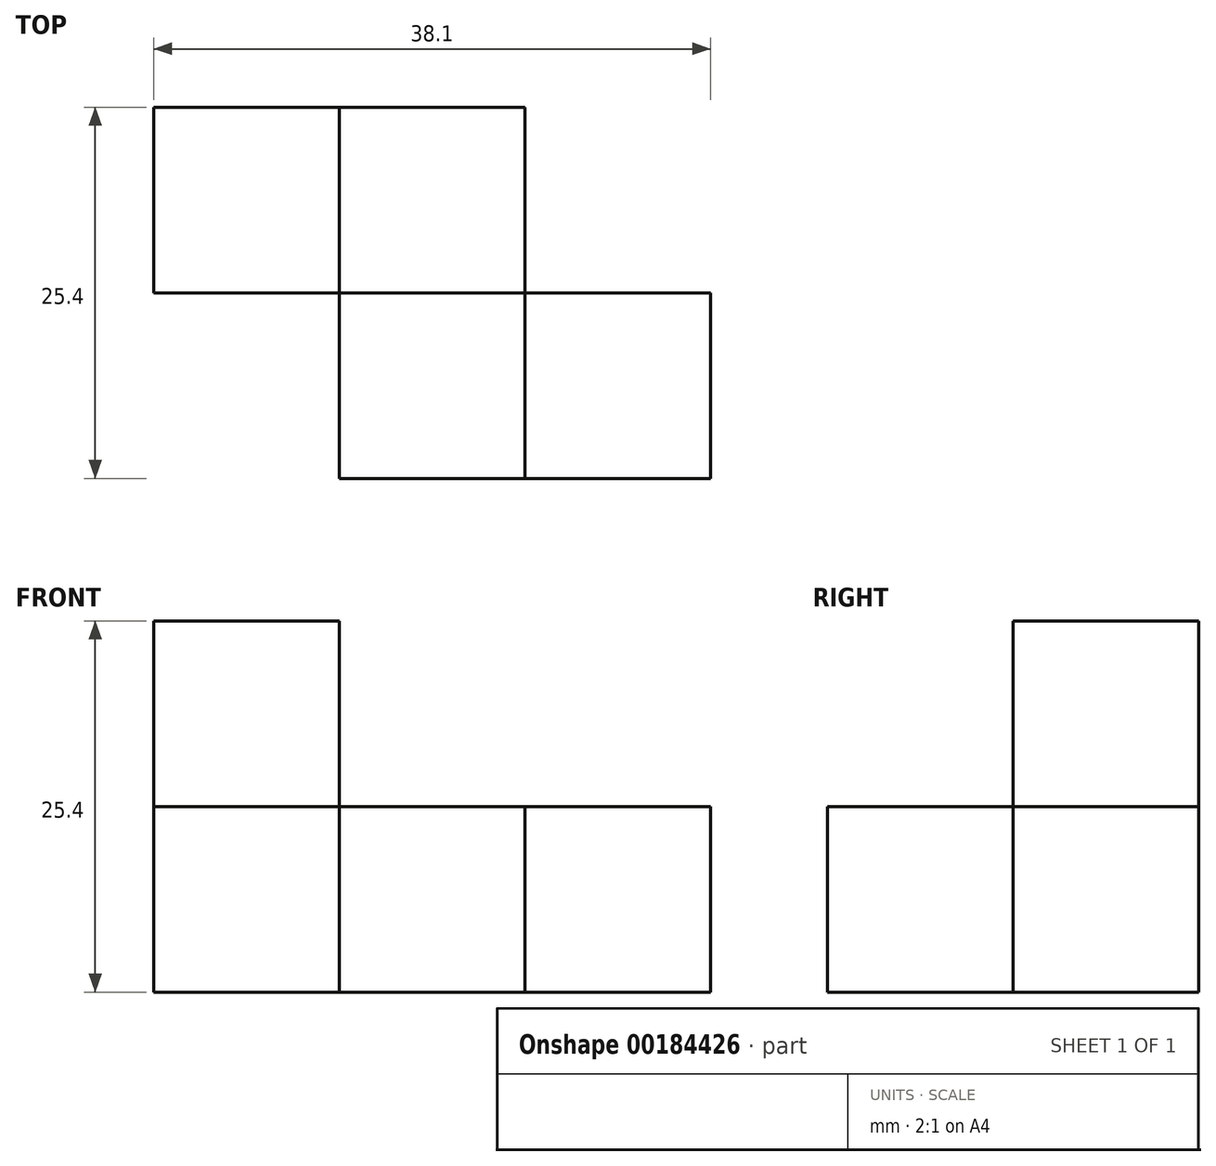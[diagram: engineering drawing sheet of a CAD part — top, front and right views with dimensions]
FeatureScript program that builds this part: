
annotation { "Feature Type Name" : "Feature", "Feature Type Description" : "" }
export const myFeature = defineFeature(function(context is Context, id is Id, definition is map)
    precondition{}
    {
        {
            var Q0;
            Q0=qCreatedBy(makeId("Front.planeOp"),FACE);
            var sketch = newSketch(context, id + "F0", { "sketchPlane" : qUnion([Q0])});
            skLineSegment(sketch, "E0.bottom", {"start": v(-58.66, 0) * mm, "end": v(-45.96, 0) * mm});
            skLineSegment(sketch, "E0.top", {"start": v(-58.66, -12.7) * mm, "end": v(-45.96, -12.7) * mm});
            skLineSegment(sketch, "E0.left", {"start": v(-58.66, 0) * mm, "end": v(-58.66, -12.7) * mm});
            skLineSegment(sketch, "E0.right", {"start": v(-45.96, 0) * mm, "end": v(-45.96, -12.7) * mm});
            skSolve(sketch);
        }
        {
            var Q0;
            Q0 = qSketchRegion(id + "F0", true);
            extrude(context, id + "F1", {"entities" : qUnion([Q0]), "depth" : 12.7 * mm});
        }
        {
            var Q0;
            Q0=makeQuery(id+"F1.opExtrude","SWEPT_EDGE",EDGE,{"disambiguationData":[OSD([sQuery(id+"F0.wireOp",EDGE,"E0.bottom"),sQuery(id+"F0.wireOp",EDGE,"E0.right")])]});
            cPoint(context, id + "F2", {"entities" : qUnion([Q0]), "parameter" : 0.5});
        }
        {
            var Q0;
            Q0=makeQuery(id+"F1.opExtrude","SWEPT_EDGE",EDGE,{"disambiguationData":[OSD([sQuery(id+"F0.wireOp",EDGE,"E0.bottom"),sQuery(id+"F0.wireOp",EDGE,"E0.left")])]});
            cPoint(context, id + "F3", {"entities" : qUnion([Q0]), "parameter" : 0.5});
        }
        {
            var Q0;
            Q0=makeQuery(id+"F1.opExtrude","SWEPT_BODY",BODY,{"disambiguationData":[OSD([sQuery(id+"F0.wireOp",EDGE,"E0.bottom"),sQuery(id+"F0.wireOp",EDGE,"E0.top"),sQuery(id+"F0.wireOp",EDGE,"E0.left"),sQuery(id+"F0.wireOp",EDGE,"E0.right")])]});
            var Q1;
            Q1 = qCreatedBy(id + "F2" ,VERTEX);
            var Q2;
            Q2 = qCreatedBy(id + "F3" ,VERTEX);
            transform(context, id + "F4", {"entities" : qUnion([Q0]), "transformType" : TransformType.TRANSLATION_ENTITY, "oppositeDirectionEntity" : false, "transformLine" : qUnion([Q1, Q2]), "makeCopy" : true});
        }
        {
            var Q0;
            Q0=makeQuery(id+"F4.opPattern","COPY",EDGE,{"derivedFrom":makeQuery(id+"F1.opExtrude","CAP_EDGE",EDGE,{"disambiguationData":[OSD([sQuery(id+"F0.wireOp",EDGE,"E0.bottom")])],"isStart":false}),"instanceName":"1"});
            cPoint(context, id + "F5", {"entities" : qUnion([Q0]), "parameter" : 0.5});
        }
        {
            var Q0;
            Q0=makeQuery(id+"F4.opPattern","COPY",EDGE,{"derivedFrom":makeQuery(id+"F1.opExtrude","CAP_EDGE",EDGE,{"disambiguationData":[OSD([sQuery(id+"F0.wireOp",EDGE,"E0.bottom")])],"isStart":true}),"instanceName":"1"});
            cPoint(context, id + "F6", {"entities" : qUnion([Q0]), "parameter" : 0.5});
        }
        {
            var Q0;
            Q0=makeQuery(id+"F4.opPattern","COPY",BODY,{"derivedFrom":makeQuery(id+"F1.opExtrude","SWEPT_BODY",BODY,{"disambiguationData":[OSD([sQuery(id+"F0.wireOp",EDGE,"E0.bottom"),sQuery(id+"F0.wireOp",EDGE,"E0.top"),sQuery(id+"F0.wireOp",EDGE,"E0.left"),sQuery(id+"F0.wireOp",EDGE,"E0.right")])]}),"instanceName":"1"});
            var Q1;
            Q1 = qCreatedBy(id + "F5" ,VERTEX);
            var Q2;
            Q2 = qCreatedBy(id + "F6" ,VERTEX);
            transform(context, id + "F7", {"entities" : qUnion([Q0]), "transformType" : TransformType.TRANSLATION_ENTITY, "oppositeDirectionEntity" : false, "transformLine" : qUnion([Q1, Q2]), "makeCopy" : true});
        }
        {
            var Q0;
            Q0=makeQuery(id+"F7.opPattern","COPY",EDGE,{"derivedFrom":makeQuery(id+"F4.opPattern","COPY",EDGE,{"derivedFrom":makeQuery(id+"F1.opExtrude","SWEPT_EDGE",EDGE,{"disambiguationData":[OSD([sQuery(id+"F0.wireOp",EDGE,"E0.bottom"),sQuery(id+"F0.wireOp",EDGE,"E0.right")])]}),"instanceName":"1"}),"instanceName":"1"});
            cPoint(context, id + "F8", {"entities" : qUnion([Q0]), "parameter" : 0.5});
        }
        {
            var Q0;
            Q0=makeQuery(id+"F7.opPattern","COPY",EDGE,{"derivedFrom":makeQuery(id+"F4.opPattern","COPY",EDGE,{"derivedFrom":makeQuery(id+"F1.opExtrude","SWEPT_EDGE",EDGE,{"disambiguationData":[OSD([sQuery(id+"F0.wireOp",EDGE,"E0.bottom"),sQuery(id+"F0.wireOp",EDGE,"E0.left")])]}),"instanceName":"1"}),"instanceName":"1"});
            cPoint(context, id + "F9", {"entities" : qUnion([Q0]), "parameter" : 0.5});
        }
        {
            var Q0;
            Q0=makeQuery(id+"F7.opPattern","COPY",BODY,{"derivedFrom":makeQuery(id+"F4.opPattern","COPY",BODY,{"derivedFrom":makeQuery(id+"F1.opExtrude","SWEPT_BODY",BODY,{"disambiguationData":[OSD([sQuery(id+"F0.wireOp",EDGE,"E0.bottom"),sQuery(id+"F0.wireOp",EDGE,"E0.top"),sQuery(id+"F0.wireOp",EDGE,"E0.left"),sQuery(id+"F0.wireOp",EDGE,"E0.right")])]}),"instanceName":"1"}),"instanceName":"1"});
            var Q1;
            Q1 = qCreatedBy(id + "F8" ,VERTEX);
            var Q2;
            Q2 = qCreatedBy(id + "F9" ,VERTEX);
            transform(context, id + "F10", {"entities" : qUnion([Q0]), "transformType" : TransformType.TRANSLATION_ENTITY, "oppositeDirectionEntity" : false, "transformLine" : qUnion([Q1, Q2]), "makeCopy" : true});
        }
        {
            var Q0;
            Q0=makeQuery(id+"F10.opPattern","COPY",BODY,{"derivedFrom":makeQuery(id+"F7.opPattern","COPY",BODY,{"derivedFrom":makeQuery(id+"F4.opPattern","COPY",BODY,{"derivedFrom":makeQuery(id+"F1.opExtrude","SWEPT_BODY",BODY,{"disambiguationData":[OSD([sQuery(id+"F0.wireOp",EDGE,"E0.bottom"),sQuery(id+"F0.wireOp",EDGE,"E0.top"),sQuery(id+"F0.wireOp",EDGE,"E0.left"),sQuery(id+"F0.wireOp",EDGE,"E0.right")])]}),"instanceName":"1"}),"instanceName":"1"}),"instanceName":"1"});
            transform(context, id + "F11", {"entities" : qUnion([Q0]), "transformType" : TransformType.TRANSLATION_3D, "dx" : 0 * mm, "dy" : 0 * mm, "dz" : 12.7 * mm, "makeCopy" : true});
        }
    });
